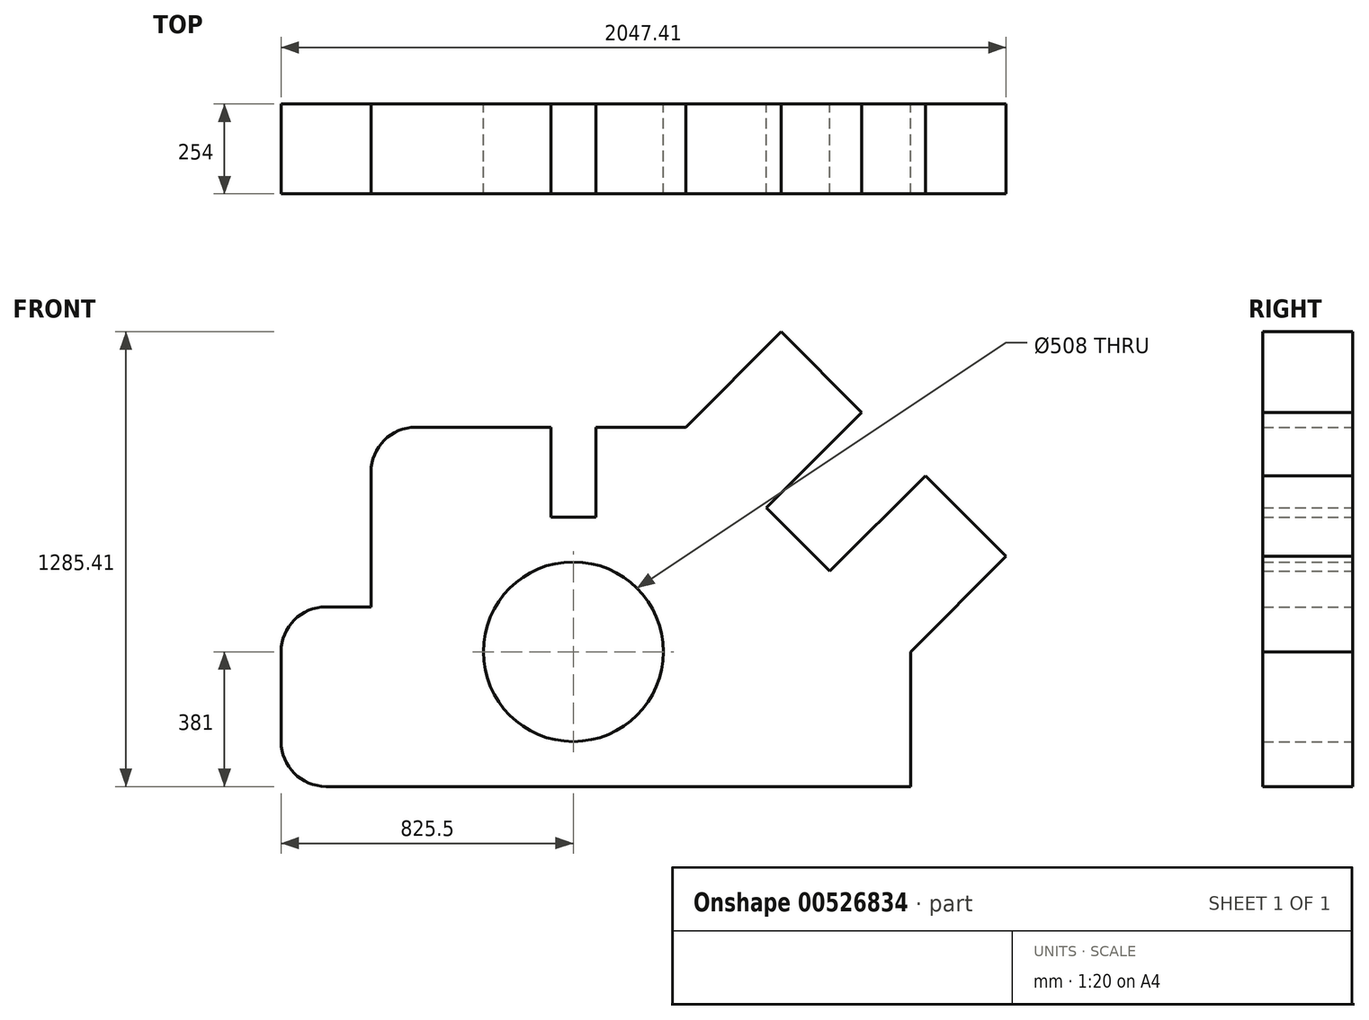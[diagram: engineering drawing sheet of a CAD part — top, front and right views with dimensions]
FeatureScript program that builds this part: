
annotation { "Feature Type Name" : "Feature", "Feature Type Description" : "" }
export const myFeature = defineFeature(function(context is Context, id is Id, definition is map)
    precondition{}
    {
        {
            var Q0;
            Q0=qCreatedBy(makeId("Front.planeOp"),FACE);
            var sketch = newSketch(context, id + "F0", { "sketchPlane" : qUnion([Q0])});
            skLineSegment(sketch, "E0", {"start": v(127, 0) * mm, "end": v(1778, 0) * mm});
            skLineSegment(sketch, "E1", {"start": v(1778, 0) * mm, "end": v(1778, 381) * mm});
            skLineSegment(sketch, "E2", {"start": v(0, 127) * mm, "end": v(0, 381) * mm});
            skCircle(sketch, "E3", {"center": v(825.5, 381) * mm, "radius": 254 * mm});
            skLineSegment(sketch, "E4", {"start": v(127, 508) * mm, "end": v(254, 508) * mm});
            skLineSegment(sketch, "E5", {"start": v(254, 508) * mm, "end": v(254, 889) * mm});
            skLineSegment(sketch, "E6", {"start": v(381, 1016) * mm, "end": v(762, 1016) * mm});
            skLineSegment(sketch, "E7", {"start": v(762, 1016) * mm, "end": v(762, 762) * mm});
            skLineSegment(sketch, "E8", {"start": v(762, 762) * mm, "end": v(889, 762) * mm});
            skLineSegment(sketch, "E9", {"start": v(889, 762) * mm, "end": v(889, 1016) * mm});
            skLineSegment(sketch, "E10", {"start": v(889, 1016) * mm, "end": v(1143, 1016) * mm});
            skLineSegment(sketch, "E11", {"start": v(1778, 381) * mm, "end": v(2047.4, 650.4) * mm});
            skLineSegment(sketch, "E12", {"start": v(2047.4, 650.4) * mm, "end": v(1819.71, 878.1) * mm});
            skLineSegment(sketch, "E13", {"start": v(1819.71, 878.1) * mm, "end": v(1550.3, 608.7) * mm});
            skLineSegment(sketch, "E14", {"start": v(1550.3, 608.7) * mm, "end": v(1370.7, 788.3) * mm});
            skLineSegment(sketch, "E15", {"start": v(1370.7, 788.3) * mm, "end": v(1640.1, 1057.71) * mm});
            skLineSegment(sketch, "E16", {"start": v(1640.1, 1057.71) * mm, "end": v(1412.4, 1285.4) * mm});
            skLineSegment(sketch, "E17", {"start": v(1412.4, 1285.4) * mm, "end": v(1143, 1016) * mm});
            skPoint(sketch, "E18.visualSharp", {"position": v(0, 0) * mm});
            skArc(sketch, "E18.filletArc", {"start": v(0, 127) * mm, "mid": v(37.2, 37.2) * mm, "end": v(127, 0) * mm});
            skPoint(sketch, "E19.visualSharp", {"position": v(0, 508) * mm});
            skArc(sketch, "E19.filletArc", {"start": v(127, 508) * mm, "mid": v(37.2, 470.8) * mm, "end": v(0, 381) * mm});
            skPoint(sketch, "E20.visualSharp", {"position": v(254, 1016) * mm});
            skArc(sketch, "E20.filletArc", {"start": v(381, 1016) * mm, "mid": v(291.2, 978.8) * mm, "end": v(254, 889) * mm});
            skSolve(sketch);
        }
        {
            var Q0;
            Q0=makeQuery(id+"F0.imprint","IMPRINT",FACE,{"disambiguationData":[TD([[makeQuery(id+"F0.imprint","IMPRINT",EDGE,{"derivedFrom":sQuery(id+"F0.wireOp",EDGE,"E0")}),1.0]])]});
            extrude(context, id + "F1", {"entities" : qUnion([Q0]), "depth" : 254 * mm, "offsetDistance" : 25.4 * mm});
        }
    });
